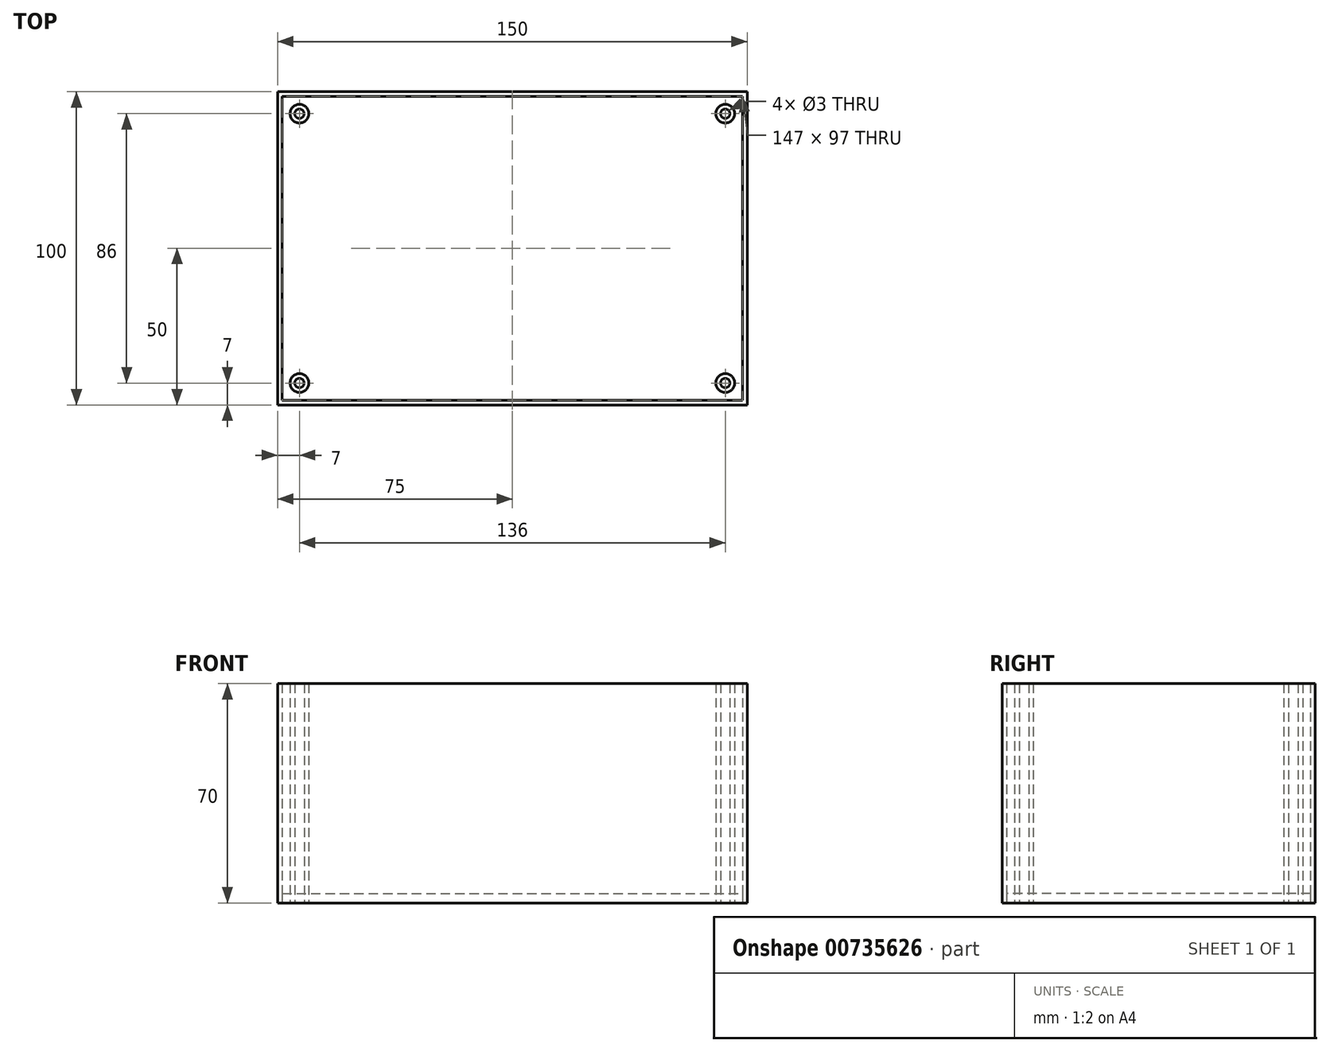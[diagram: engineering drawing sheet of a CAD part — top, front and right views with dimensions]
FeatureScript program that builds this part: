
annotation { "Feature Type Name" : "Feature", "Feature Type Description" : "" }
export const myFeature = defineFeature(function(context is Context, id is Id, definition is map)
    precondition{}
    {
        {
            var Q0;
            Q0=qCreatedBy(makeId("Top.planeOp"),FACE);
            var sketch = newSketch(context, id + "F0", { "sketchPlane" : qUnion([Q0])});
            skLineSegment(sketch, "E0.bottom", {"start": v(75, -50) * mm, "end": v(-75, -50) * mm});
            skLineSegment(sketch, "E0.top", {"start": v(75, 50) * mm, "end": v(-75, 50) * mm});
            skLineSegment(sketch, "E0.left", {"start": v(75, -50) * mm, "end": v(75, 50) * mm});
            skLineSegment(sketch, "E0.right", {"start": v(-75, -50) * mm, "end": v(-75, 50) * mm});
            skPoint(sketch, "E0.middle", {"position": v(0, 0) * mm});
            skCircle(sketch, "E1", {"center": v(-68, 43) * mm, "radius": 1.5 * mm});
            skLineSegment(sketch, "E2.bottom", {"start": v(-73.5, 48.5) * mm, "end": v(73.5, 48.5) * mm});
            skLineSegment(sketch, "E2.top", {"start": v(-73.5, -48.5) * mm, "end": v(73.5, -48.5) * mm});
            skLineSegment(sketch, "E2.left", {"start": v(-73.5, 48.5) * mm, "end": v(-73.5, -48.5) * mm});
            skLineSegment(sketch, "E2.right", {"start": v(73.5, 48.5) * mm, "end": v(73.5, -48.5) * mm});
            skCircle(sketch, "E3", {"center": v(-68, 43) * mm, "radius": 3 * mm});
            skSolve(sketch);
        }
        {
            var Q0;
            Q0=makeQuery(id+"F0.imprint","IMPRINT",FACE,{"disambiguationData":[TD([[makeQuery(id+"F0.imprint","IMPRINT",EDGE,{"derivedFrom":sQuery(id+"F0.wireOp",EDGE,"E0.bottom")}),-1.0]])]});
            var Q1;
            Q1=makeQuery(id+"F0.imprint","IMPRINT",FACE,{"disambiguationData":[TD([[makeQuery(id+"F0.imprint","IMPRINT",EDGE,{"derivedFrom":sQuery(id+"F0.wireOp",EDGE,"E1")}),-1.0]])]});
            extrude(context, id + "F1", {"entities" : qUnion([Q0, Q1]), "depth" : 70 * mm, "offsetDistance" : 25 * mm});
        }
        {
            var Q0;
            Q0=qCreatedBy(makeId("Top.planeOp"),FACE);
            var sketch = newSketch(context, id + "F2", { "sketchPlane" : qUnion([Q0])});
            skLineSegment(sketch, "E4.bottom", {"start": v(-73.5, 48.5) * mm, "end": v(73.5, 48.5) * mm});
            skLineSegment(sketch, "E4.top", {"start": v(-73.5, -48.5) * mm, "end": v(73.5, -48.5) * mm});
            skLineSegment(sketch, "E4.left", {"start": v(-73.5, 48.5) * mm, "end": v(-73.5, -48.5) * mm});
            skLineSegment(sketch, "E4.right", {"start": v(73.5, 48.5) * mm, "end": v(73.5, -48.5) * mm});
            skPoint(sketch, "E4.middle", {"position": v(0, 0) * mm});
            skSolve(sketch);
        }
        {
            var Q0;
            Q0=makeQuery(id+"F2.imprint","IMPRINT",FACE,{"disambiguationData":[TD([[makeQuery(id+"F2.imprint","IMPRINT",EDGE,{"derivedFrom":sQuery(id+"F2.wireOp",EDGE,"E4.bottom")}),-1.0]])]});
            extrude(context, id + "F3", {"entities" : qUnion([Q0]), "depth" : 3 * mm, "offsetDistance" : 25 * mm});
        }
        {
            var Q0;
            Q0=makeQuery(id+"F1.opExtrude","SWEPT_BODY",BODY,{"disambiguationData":[OSD([sQuery(id+"F0.wireOp",EDGE,"E1"),sQuery(id+"F0.wireOp",EDGE,"E3")])]});
            transform(context, id + "F4", {"entities" : qUnion([Q0]), "transformType" : TransformType.TRANSLATION_3D, "dx" : 0 * mm, "dy" : -86 * mm, "dz" : 0 * mm, "makeCopy" : true});
        }
        {
            var Q0;
            Q0=makeQuery(id+"F1.opExtrude","SWEPT_BODY",BODY,{"disambiguationData":[OSD([sQuery(id+"F0.wireOp",EDGE,"E1"),sQuery(id+"F0.wireOp",EDGE,"E3")])]});
            transform(context, id + "F5", {"entities" : qUnion([Q0]), "transformType" : TransformType.TRANSLATION_3D, "dx" : 136 * mm, "dy" : 0 * mm, "dz" : 0 * mm, "makeCopy" : true});
        }
        {
            var Q0;
            Q0=makeQuery(id+"F4.opPattern","COPY",BODY,{"derivedFrom":makeQuery(id+"F1.opExtrude","SWEPT_BODY",BODY,{"disambiguationData":[OSD([sQuery(id+"F0.wireOp",EDGE,"E1"),sQuery(id+"F0.wireOp",EDGE,"E3")])]}),"instanceName":"1"});
            transform(context, id + "F6", {"entities" : qUnion([Q0]), "transformType" : TransformType.TRANSLATION_3D, "dx" : 136 * mm, "dy" : 0 * mm, "dz" : 0 * mm, "makeCopy" : true});
        }
    });
